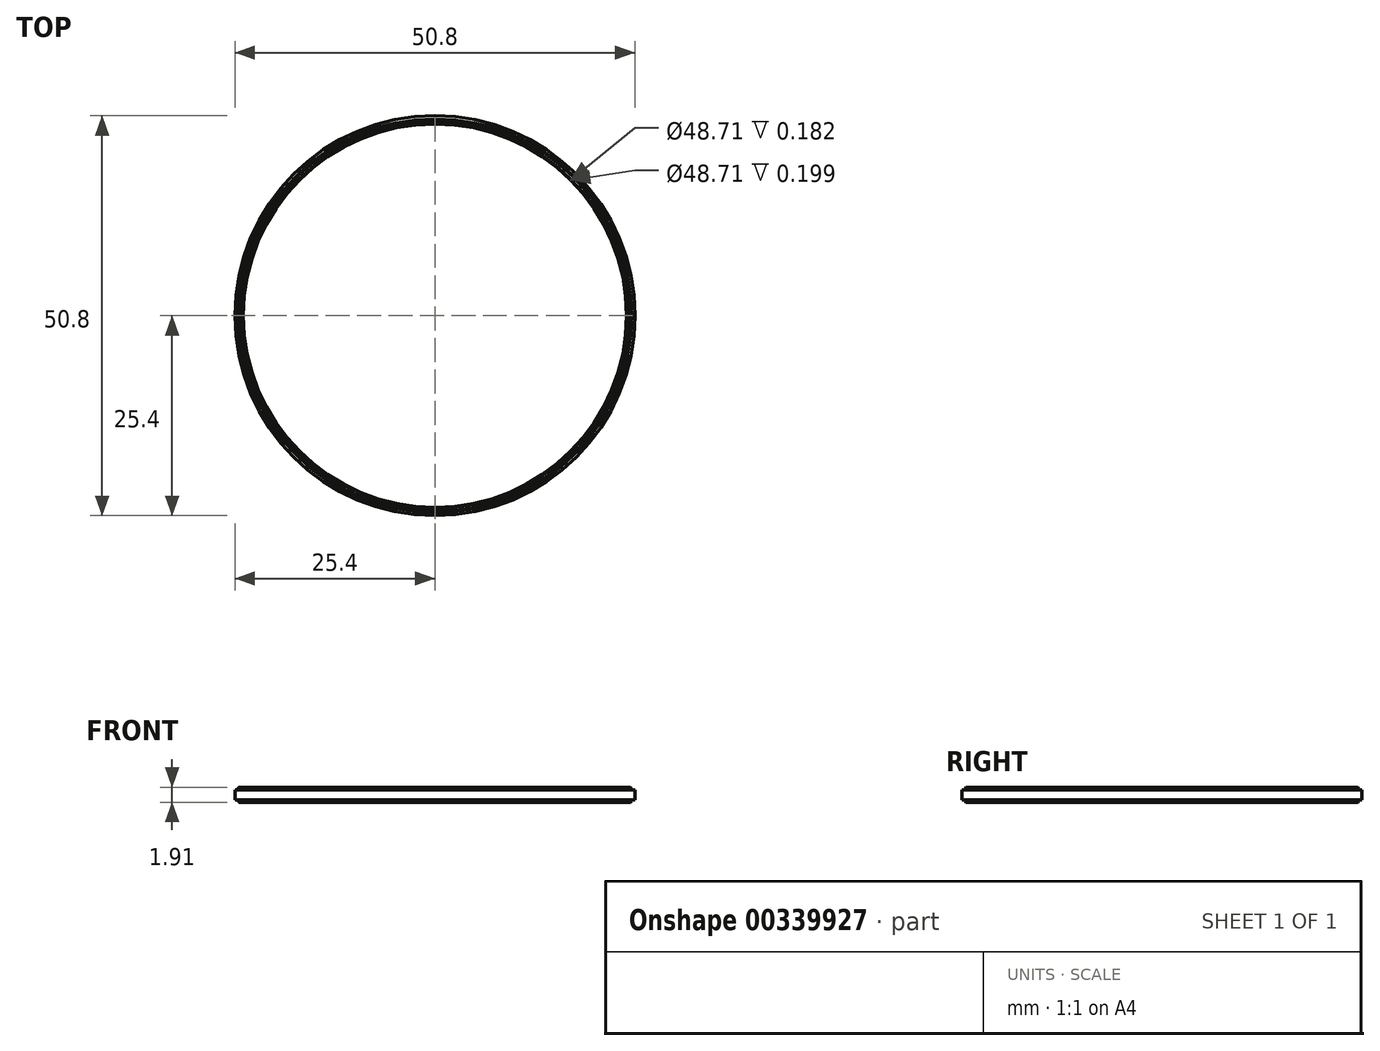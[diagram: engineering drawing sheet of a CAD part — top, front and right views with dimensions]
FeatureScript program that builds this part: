
annotation { "Feature Type Name" : "Feature", "Feature Type Description" : "" }
export const myFeature = defineFeature(function(context is Context, id is Id, definition is map)
    precondition{}
    {
        {
            var Q0;
            Q0=qCreatedBy(makeId("Front.planeOp"),FACE);
            var sketch = newSketch(context, id + "F0", { "sketchPlane" : qUnion([Q0])});
            skLineSegment(sketch, "E0.bottom", {"start": v(0, 4.57) * mm, "end": v(25.4, 4.57) * mm});
            skLineSegment(sketch, "E0.top", {"start": v(0, 5.84) * mm, "end": v(25.4, 5.84) * mm});
            skLineSegment(sketch, "E0.left", {"start": v(0, 4.57) * mm, "end": v(0, 5.84) * mm});
            skLineSegment(sketch, "E0.right", {"start": v(25.4, 4.57) * mm, "end": v(25.4, 5.84) * mm});
            skLineSegment(sketch, "E1.bottom", {"start": v(24.36, 6.17) * mm, "end": v(25, 6.17) * mm});
            skLineSegment(sketch, "E1.top", {"start": v(24.36, 4.26) * mm, "end": v(25, 4.26) * mm});
            skLineSegment(sketch, "E1.left", {"start": v(24.36, 6.17) * mm, "end": v(24.36, 4.26) * mm});
            skLineSegment(sketch, "E1.right", {"start": v(25, 6.17) * mm, "end": v(25, 4.26) * mm});
            skSolve(sketch);
        }
        {
            var Q0;
            {var subQ0=sQuery(id+"F0.wireOp",EDGE,"E0.left");Q0=makeQuery(id+"F0.imprint","IMPRINT",FACE,{"disambiguationData":[TD([[makeQuery(id+"F0.imprint","IMPRINT",EDGE,{"derivedFrom":subQ0}),-1.0]])]});}
            var Q1;
            {var subQ0=sQuery(id+"F0.wireOp",EDGE,"E1.left");var subQ1=sQuery(id+"F0.wireOp",EDGE,"E0.bottom");var subQ2=makeQuery(id+"F0.imprint","INTERSECT",VERTEX,{"derivedFrom":[subQ1,subQ0]});Q1=makeQuery(id+"F0.imprint","IMPRINT",FACE,{"disambiguationData":[TD([[makeQuery(id+"F0.imprint","IMPRINT",EDGE,{"disambiguationData":[TD([[subQ2,-1.0]])],"derivedFrom":subQ1}),1.0]])]});}
            var Q2;
            {var subQ0=sQuery(id+"F0.wireOp",EDGE,"E0.right");Q2=makeQuery(id+"F0.imprint","IMPRINT",FACE,{"disambiguationData":[TD([[makeQuery(id+"F0.imprint","IMPRINT",EDGE,{"derivedFrom":subQ0}),1.0]])]});}
            var Q3;
            {var subQ5=sQuery(id+"F0.wireOp",EDGE,"E1.bottom");Q3=makeQuery(id+"F0.imprint","IMPRINT",FACE,{"disambiguationData":[TD([[makeQuery(id+"F0.imprint","IMPRINT",EDGE,{"derivedFrom":subQ5}),-1.0]])]});}
            var Q4;
            {var subQ5=sQuery(id+"F0.wireOp",EDGE,"E1.top");Q4=makeQuery(id+"F0.imprint","IMPRINT",FACE,{"disambiguationData":[TD([[makeQuery(id+"F0.imprint","IMPRINT",EDGE,{"derivedFrom":subQ5}),1.0]])]});}
            var Q5;
            Q5=sQuery(id+"F0.wireOp",EDGE,"E0.left");
            revolve(context, id + "F1", {"entities" : qUnion([Q0, Q1, Q2, Q3, Q4]), "axis" : qUnion([Q5]), "revolveType" : RevolveType.FULL});
        }
        {
            var Q0;
            Q0=makeQuery(id+"F1.opRevolve","SWEPT_EDGE",EDGE,{"disambiguationData":[OSD([sQuery(id+"F0.wireOp",EDGE,"E1.bottom"),sQuery(id+"F0.wireOp",EDGE,"E1.right")])]});
            chamfer(context, id + "F2", {"entities" : qUnion([Q0]), "width" : 0.13 * mm, "tangentPropagation" : true});
        }
        {
            var Q0;
            Q0=makeQuery(id+"F1.opRevolve","SWEPT_EDGE",EDGE,{"disambiguationData":[OSD([sQuery(id+"F0.wireOp",EDGE,"E1.bottom"),sQuery(id+"F0.wireOp",EDGE,"E1.left")])]});
            chamfer(context, id + "F3", {"entities" : qUnion([Q0]), "width" : 0.13 * mm, "tangentPropagation" : true});
        }
        {
            var Q0;
            Q0=makeQuery(id+"F1.opRevolve","SWEPT_EDGE",EDGE,{"disambiguationData":[OSD([sQuery(id+"F0.wireOp",EDGE,"E1.top"),sQuery(id+"F0.wireOp",EDGE,"E1.right")])]});
            chamfer(context, id + "F4", {"entities" : qUnion([Q0]), "width" : 0.13 * mm, "tangentPropagation" : true});
        }
        {
            var Q0;
            Q0=makeQuery(id+"F1.opRevolve","SWEPT_EDGE",EDGE,{"disambiguationData":[OSD([sQuery(id+"F0.wireOp",EDGE,"E1.top"),sQuery(id+"F0.wireOp",EDGE,"E1.left")])]});
            chamfer(context, id + "F5", {"entities" : qUnion([Q0]), "width" : 0.13 * mm, "tangentPropagation" : true});
        }
    });
